# Revit family: 304_515a6fb074064c82869df4a29a1655
name_source: partatom
category: Pipe Accessories
revit_build: Autodesk Revit 2018 (Build: 20170223_1515(x64)
units: mm (PartAtom-declared; Revit-internal decimal feet)

## family parameters
Always vertical = Yes
Cut with Voids When Loaded = No
Part Type = Valve - Breaks Into
Round Connector Dimension = Use Diameter
Shared = No
Work Plane-Based = No

## types (16) — shared parameters
Description = DZR brass automatic balancing valve PN25
H5 = 2 mm  [stored 0.00656168 ft]
H6 = 2 mm  [stored 0.00656168 ft]
H8 = 34 mm  [stored 0.111549 ft]
L2D = 96 mm
L2D_Min = 3048 mm
Manufacturer = VIR
QmdConnectorList = 301;D;302;D
R6 = 8 mm  [stored 0.0262467 ft]
R7 = 9 mm  [stored 0.0295276 ft]
URL = http://www.vironline.com
W2D = 15 mm  [stored 0.0492126 ft]
magiPartTypeId = 304
magiProductFamilyId = 515a6fb074064c82869df4a29a1655
zero-valued in all types: L4

## per-type parameters (varying)
| type | CenSd_R2_6 | CenSd_R3_6 | D | H7 | L2 | L2__ve | L3 | L3__ve | L6 | L7 | L_2 | R1 | R2 | R3 | W1 | magiProductId |
| 9905V DN15 | 12 mm  [stored 0.0393701 ft] | 8 mm  [stored 0.0262467 ft] | 15 mm | 24 mm  [stored 0.0787402 ft] | 12 mm  [stored 0.0393701 ft] | -12 mm | 7 mm | -7 mm | 9 mm  [stored 0.0295276 ft] | 9 mm  [stored 0.0295276 ft] | 48 mm | 9 mm  [stored 0.0295276 ft] | 14 mm  [stored 0.0459318 ft] | 10 mm  [stored 0.0328084 ft] | 5 mm  [stored 0.0164042 ft] | 188080d5addc40818d4c0d6fd8fd4a |
| 9905V DN15-H HP range | 12 mm  [stored 0.0393701 ft] | 8 mm  [stored 0.0262467 ft] | 15 mm | 31 mm | 13 mm  [stored 0.0426509 ft] | -13 mm | 8 mm  [stored 0.0262467 ft] | -8 mm | 13 mm  [stored 0.0426509 ft] | 13 mm  [stored 0.0426509 ft] | 55 mm | 9 mm  [stored 0.0295276 ft] | 14 mm  [stored 0.0459318 ft] | 10 mm  [stored 0.0328084 ft] | 0 mm  [stored 0 ft] | 8e05195c886c4b93baffe8caef213a |
| 9905V DN15-H STD range | 12 mm  [stored 0.0393701 ft] | 8 mm  [stored 0.0262467 ft] | 15 mm | 31 mm | 13 mm  [stored 0.0426509 ft] | -13 mm | 8 mm  [stored 0.0262467 ft] | -8 mm | 13 mm  [stored 0.0426509 ft] | 13 mm  [stored 0.0426509 ft] | 55 mm | 9 mm  [stored 0.0295276 ft] | 14 mm  [stored 0.0459318 ft] | 10 mm  [stored 0.0328084 ft] | 0 mm  [stored 0 ft] | 006dcdb2222242708e9bba8282151b |
| 9905V DN20 HP range | 16 mm | 11 mm | 20 mm | 31 mm | 14 mm  [stored 0.0459318 ft] | -14 mm | 8 mm  [stored 0.0262467 ft] | -8 mm | 14 mm  [stored 0.0459318 ft] | 14 mm  [stored 0.0459318 ft] | 58 mm | 12 mm  [stored 0.0393701 ft] | 18 mm  [stored 0.0590551 ft] | 13 mm  [stored 0.0426509 ft] | 0 mm  [stored 0 ft] | 2760a5ecb5324894b4c355b567ee4c |
| 9905V DN20 STD range | 16 mm | 11 mm | 20 mm | 31 mm | 14 mm  [stored 0.0459318 ft] | -14 mm | 8 mm  [stored 0.0262467 ft] | -8 mm | 14 mm  [stored 0.0459318 ft] | 14 mm  [stored 0.0459318 ft] | 58 mm | 12 mm  [stored 0.0393701 ft] | 18 mm  [stored 0.0590551 ft] | 13 mm  [stored 0.0426509 ft] | 0 mm  [stored 0 ft] | a93b5699ea4a47a092e3a6307decac |
| 9905V DN20-L | 16 mm | 11 mm | 20 mm | 24 mm  [stored 0.0787402 ft] | 14 mm  [stored 0.0459318 ft] | -14 mm | 8 mm  [stored 0.0262467 ft] | -8 mm | 10 mm  [stored 0.0328084 ft] | 10 mm  [stored 0.0328084 ft] | 58 mm | 12 mm  [stored 0.0393701 ft] | 18 mm  [stored 0.0590551 ft] | 13 mm  [stored 0.0426509 ft] | 5 mm  [stored 0.0164042 ft] | 801f8a9d800343f8bec7a4ee61902f |
| 9905V DN25 HP range | 19 mm | 14 mm  [stored 0.0459318 ft] | 25 mm | 31 mm | 15 mm  [stored 0.0492126 ft] | -15 mm | 9 mm  [stored 0.0295276 ft] | -9 mm  [stored -0.0295276 ft] | 14 mm  [stored 0.0459318 ft] | 14 mm  [stored 0.0459318 ft] | 60 mm | 15 mm  [stored 0.0492126 ft] | 23 mm | 16 mm | 0 mm  [stored 0 ft] | dffada7d982143a0aaef9cd863a75c |
| 9905V DN25 STD range | 19 mm | 14 mm  [stored 0.0459318 ft] | 25 mm | 31 mm | 15 mm  [stored 0.0492126 ft] | -15 mm | 9 mm  [stored 0.0295276 ft] | -9 mm  [stored -0.0295276 ft] | 14 mm  [stored 0.0459318 ft] | 14 mm  [stored 0.0459318 ft] | 60 mm | 15 mm  [stored 0.0492126 ft] | 23 mm | 16 mm | 0 mm  [stored 0 ft] | 70c4aa12b20d4354b83f50c62d0840 |
| 9905V DN32 HP range | 25 mm  [stored 0.082021 ft] | 18 mm  [stored 0.0590551 ft] | 32 mm | 37 mm | 20 mm  [stored 0.0656168 ft] | -20 mm  [stored -0.0656168 ft] | 12 mm  [stored 0.0393701 ft] | -12 mm | 20 mm  [stored 0.0656168 ft] | 20 mm  [stored 0.0656168 ft] | 82 mm | 19 mm | 29 mm | 21 mm | 0 mm  [stored 0 ft] | 1fc5a7413bf54c2d981a415fb2c766 |
| 9905V DN32 STD range | 25 mm  [stored 0.082021 ft] | 18 mm  [stored 0.0590551 ft] | 32 mm | 37 mm | 20 mm  [stored 0.0656168 ft] | -20 mm  [stored -0.0656168 ft] | 12 mm  [stored 0.0393701 ft] | -12 mm | 20 mm  [stored 0.0656168 ft] | 20 mm  [stored 0.0656168 ft] | 82 mm | 19 mm | 29 mm | 21 mm | 0 mm  [stored 0 ft] | 6410a77f34dd4c6986c2f354fb5902 |
| 9905V DN40 HP range | 31 mm | 23 mm | 40 mm | 37 mm | 20 mm  [stored 0.0656168 ft] | -20 mm  [stored -0.0656168 ft] | 12 mm  [stored 0.0393701 ft] | -12 mm | 20 mm  [stored 0.0656168 ft] | 20 mm  [stored 0.0656168 ft] | 82 mm | 24 mm  [stored 0.0787402 ft] | 36 mm | 26 mm  [stored 0.0853018 ft] | 0 mm  [stored 0 ft] | 90a7f69322da48c993d2b16b607b6f |
| 9905V DN40 STD range | 31 mm | 23 mm | 40 mm | 37 mm | 20 mm  [stored 0.0656168 ft] | -20 mm  [stored -0.0656168 ft] | 12 mm  [stored 0.0393701 ft] | -12 mm | 20 mm  [stored 0.0656168 ft] | 20 mm  [stored 0.0656168 ft] | 82 mm | 24 mm  [stored 0.0787402 ft] | 36 mm | 26 mm  [stored 0.0853018 ft] | 0 mm  [stored 0 ft] | 6a12a88802a94802a5991b1d26c849 |
| 9905V DN50 HP range | 39 mm | 28 mm | 50 mm | 37 mm | 25 mm  [stored 0.082021 ft] | -25 mm | 15 mm  [stored 0.0492126 ft] | -15 mm | 25 mm  [stored 0.082021 ft] | 25 mm  [stored 0.082021 ft] | 104 mm | 30 mm  [stored 0.0984252 ft] | 45 mm | 33 mm | 0 mm  [stored 0 ft] | bb42ac3f38de4fd2a3585f982603e1 |
| 9905V DN50 STD range | 39 mm | 28 mm | 50 mm | 37 mm | 25 mm  [stored 0.082021 ft] | -25 mm | 15 mm  [stored 0.0492126 ft] | -15 mm | 25 mm  [stored 0.082021 ft] | 25 mm  [stored 0.082021 ft] | 104 mm | 30 mm  [stored 0.0984252 ft] | 45 mm | 33 mm | 0 mm  [stored 0 ft] | 79168a6d15994bd8bd4689a536a7b7 |
| 9905V DN50-H | 39 mm | 28 mm | 50 mm | 56 mm | 28 mm | -28 mm | 17 mm | -17 mm | 28 mm | 28 mm | 117 mm | 30 mm  [stored 0.0984252 ft] | 45 mm | 33 mm | 0 mm  [stored 0 ft] | 6ba775c8649e47af80e103c5f69afb |
| 9905V DN65 | 51 mm | 37 mm | 65 mm | 56 mm | 29 mm | -29 mm | 17 mm | -17 mm | 29 mm | 29 mm | 121 mm | 39 mm | 59 mm | 42 mm | 0 mm  [stored 0 ft] | f61df57700c5491eb1c0a3f46dd221 |

note: column(s) folded — value = type name in every type: MC Product Code

note: [stored X ft] marks values corroborated as IEEE doubles in the binary element streams (Revit-internal decimal feet)

## geometry (parser evidence)
native form markers: Sweep x1
no freeform markers — native parametric forms only
